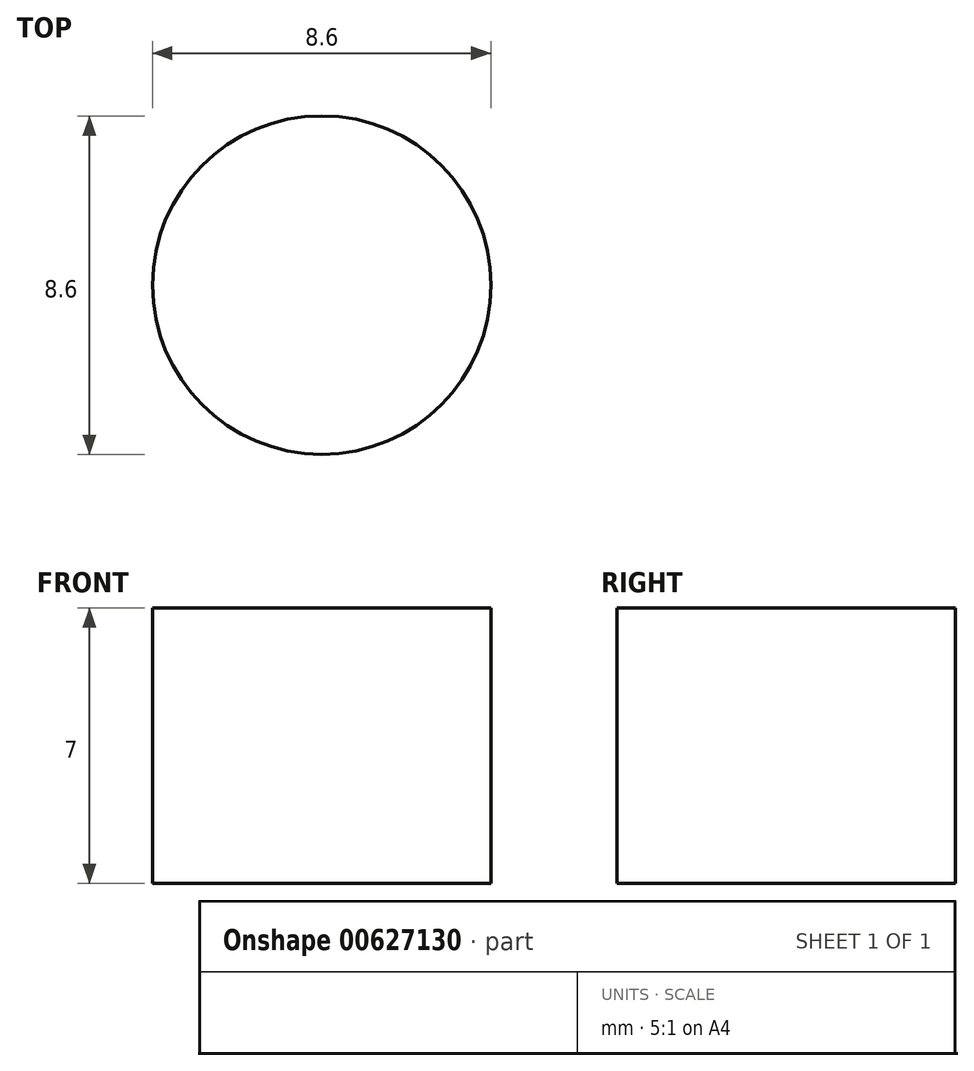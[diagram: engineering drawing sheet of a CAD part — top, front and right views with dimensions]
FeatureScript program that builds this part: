
annotation { "Feature Type Name" : "Feature", "Feature Type Description" : "" }
export const myFeature = defineFeature(function(context is Context, id is Id, definition is map)
    precondition{}
    {
        {
            var Q0;
            Q0=qCreatedBy(makeId("Top.planeOp"),FACE);
            var sketch = newSketch(context, id + "F0", { "sketchPlane" : qUnion([Q0])});
            skCircle(sketch, "E0", {"center": v(0, 0) * mm, "radius": 15.04 * mm});
            skPoint(sketch, "E1", {"position": v(-15.04, 0) * mm});
            skPoint(sketch, "E2", {"position": v(15.04, 0) * mm});
            skPoint(sketch, "E3", {"position": v(-10.53, 10.74) * mm});
            skPoint(sketch, "E4", {"position": v(10.53, 10.74) * mm});
            skLineSegment(sketch, "E5", {"start": v(10.53, 10.74) * mm, "end": v(30.38, 14.26) * mm});
            skLineSegment(sketch, "E6", {"start": v(30.38, 14.26) * mm, "end": v(15.04, 0) * mm});
            skLineSegment(sketch, "E7", {"start": v(-10.53, 10.74) * mm, "end": v(-32.95, 14.26) * mm});
            skLineSegment(sketch, "E8", {"start": v(-32.95, 14.26) * mm, "end": v(-15.04, 0) * mm});
            skEllipse(sketch, "E9", {"center": v(0, -52.48) * mm, "majorRadius": 52.48 * mm, "minorRadius": 18.24 * mm, "majorAxis": v(0, 1)});
            skLineSegment(sketch, "E10", {"start": v(-18.22, -55.34) * mm, "end": v(18.22, -55.34) * mm});
            skCircle(sketch, "E11", {"center": v(17.5, -37.59) * mm, "radius": 4.3 * mm});
            skCircle(sketch, "E12.MirrorC", {"center": v(-17.5, -37.59) * mm, "radius": 4.3 * mm});
            skCircle(sketch, "E13", {"center": v(0, 10.95) * mm, "radius": 1.6 * mm});
            skSolve(sketch);
        }
        {
            var Q0;
            {var subQ0=sQuery(id+"F0.wireOp",EDGE,"E11");var subQ1=sQuery(id+"F0.wireOp",EDGE,"E9");var subQ2=makeQuery(id+"F0.imprint","INTERSECT",VERTEX,{"disambiguationData":[OD(0.0)],"derivedFrom":[subQ1,subQ0]});Q0=makeQuery(id+"F0.imprint","IMPRINT",FACE,{"disambiguationData":[TD([[makeQuery(id+"F0.imprint","IMPRINT",EDGE,{"disambiguationData":[TD([[subQ2,-1.0]])],"derivedFrom":subQ1}),-1.0]])]});}
            var Q1;
            {var subQ0=sQuery(id+"F0.wireOp",EDGE,"E11");var subQ1=sQuery(id+"F0.wireOp",EDGE,"E9");var subQ2=makeQuery(id+"F0.imprint","INTERSECT",VERTEX,{"disambiguationData":[OD(0.0)],"derivedFrom":[subQ1,subQ0]});Q1=makeQuery(id+"F0.imprint","IMPRINT",FACE,{"disambiguationData":[TD([[makeQuery(id+"F0.imprint","IMPRINT",EDGE,{"disambiguationData":[TD([[subQ2,-1.0]])],"derivedFrom":subQ1}),1.0]])]});}
            extrude(context, id + "F1", {"entities" : qUnion([Q0, Q1]), "depth" : 7 * mm, "offsetDistance" : 25 * mm});
        }
    });
